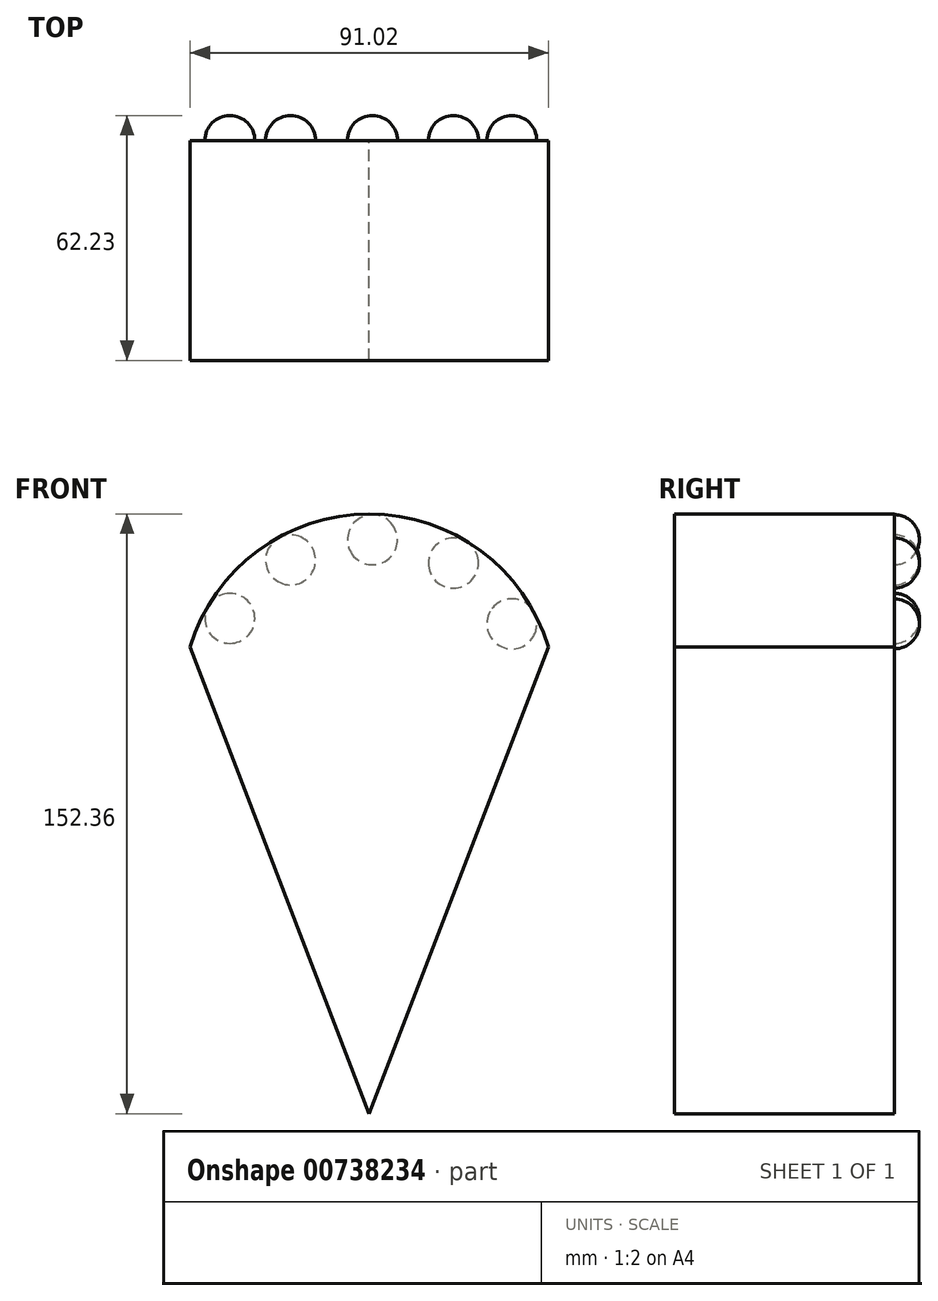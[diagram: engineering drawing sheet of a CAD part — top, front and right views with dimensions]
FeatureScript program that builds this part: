
annotation { "Feature Type Name" : "Feature", "Feature Type Description" : "" }
export const myFeature = defineFeature(function(context is Context, id is Id, definition is map)
    precondition{}
    {
        {
            var Q0;
            Q0=qCreatedBy(makeId("Front.planeOp"),FACE);
            var sketch = newSketch(context, id + "F0", { "sketchPlane" : qUnion([Q0])});
            skLineSegment(sketch, "E0", {"start": v(0, 0) * mm, "end": v(45.5, 118.57) * mm});
            skLineSegment(sketch, "E1", {"start": v(-45.5, 118.57) * mm, "end": v(0, 0) * mm});
            skArc(sketch, "E2", {"start": v(45.5, 118.57) * mm, "mid": v(0, 152.36) * mm, "end": v(-45.5, 118.57) * mm});
            skSolve(sketch);
        }
        {
            var Q0;
            Q0 = qSketchRegion(id + "F0", true);
            extrude(context, id + "F1", {"entities" : qUnion([Q0]), "depth" : 55.88 * mm, "offsetDistance" : 25.4 * mm});
        }
        {
            var Q0;
            Q0=makeQuery(id+"F1.opExtrude","CAP_FACE",FACE,{"disambiguationData":[OSD([sQuery(id+"F0.wireOp",EDGE,"E0"),sQuery(id+"F0.wireOp",EDGE,"E1"),sQuery(id+"F0.wireOp",EDGE,"E2")])],"isStart":true});
            var sketch = newSketch(context, id + "F2", { "sketchPlane" : qUnion([Q0])});
            skLineSegment(sketch, "E3", {"start": v(-45.5, 118.57) * mm, "end": v(45.5, 118.57) * mm, "construction": true});
            skLineSegment(sketch, "E4", {"start": v(35.42, 125.84) * mm, "end": v(0, 118.57) * mm, "construction": true});
            skLineSegment(sketch, "E5", {"start": v(35.42, 132.19) * mm, "end": v(35.42, 119.49) * mm});
            skArc(sketch, "E6", {"start": v(35.42, 119.49) * mm, "mid": v(41.77, 125.84) * mm, "end": v(35.42, 132.19) * mm});
            skSolve(sketch);
        }
        {
            var Q0;
            Q0 = qSketchRegion(id + "F2", true);
            var Q1;
            Q1=sQuery(id+"F2.wireOp",EDGE,"E5");
            revolve(context, id + "F3", {"surfaceOperationType" : NewSurfaceOperationType.NEW, "entities" : qUnion([Q0]), "axis" : qUnion([Q1]), "revolveType" : RevolveType.ONE_DIRECTION, "angle" : 180 * degree});
        }
        {
            var Q0;
            Q0=qCreatedBy(makeId("Right.planeOp"),FACE);
            var sketch = newSketch(context, id + "F4", { "sketchPlane" : qUnion([Q0])});
            skLineSegment(sketch, "E7", {"start": v(0, 104.46) * mm, "end": v(41.53, 104.46) * mm, "construction": true});
            skSolve(sketch);
        }
        {
            var Q0;
            Q0=makeQuery(id+"F3.opRevolve","SWEPT_BODY",BODY,{"disambiguationData":[OSD([sQuery(id+"F2.wireOp",EDGE,"E5"),sQuery(id+"F2.wireOp",EDGE,"E6")])]});
            var Q1;
            Q1=sQuery(id+"F4.wireOp",EDGE,"E7");
            circularPattern(context, id + "F5", {"entities" : qUnion([Q0]), "axis" : qUnion([Q1]), "angle" : 120 * degree, "instanceCount" : 5, "equalSpace" : true});
        }
    });
